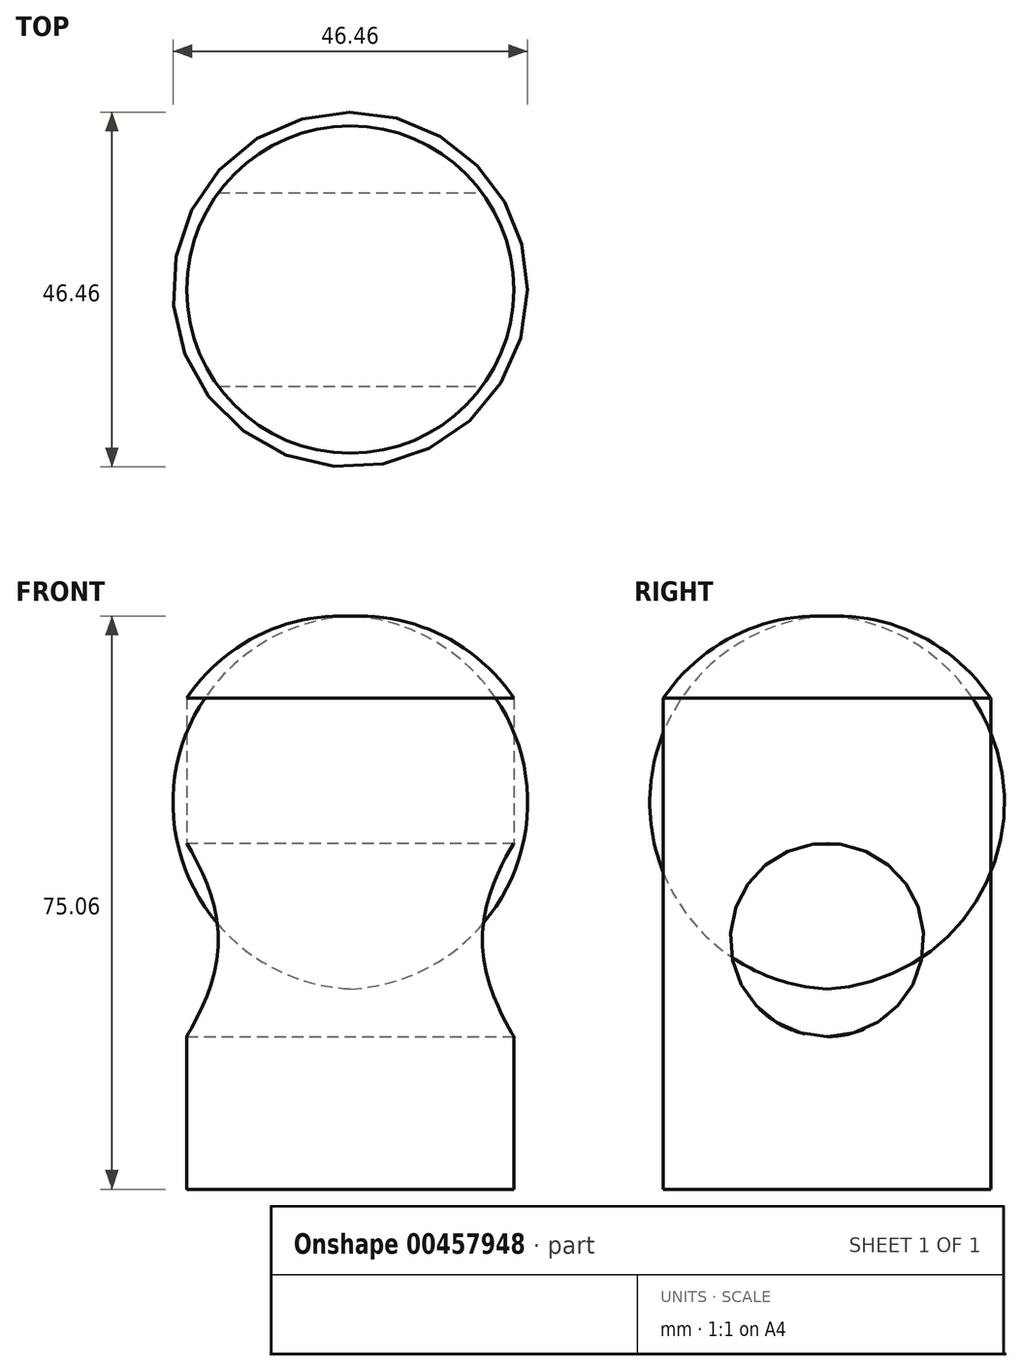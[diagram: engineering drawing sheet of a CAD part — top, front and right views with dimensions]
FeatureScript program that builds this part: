
annotation { "Feature Type Name" : "Feature", "Feature Type Description" : "" }
export const myFeature = defineFeature(function(context is Context, id is Id, definition is map)
    precondition{}
    {
        {
            var Q0;
            Q0=qCreatedBy(makeId("Front.planeOp"),FACE);
            var sketch = newSketch(context, id + "F0", { "sketchPlane" : qUnion([Q0])});
            skLineSegment(sketch, "E0", {"start": v(0, 31.65) * mm, "end": v(0, -32.66) * mm});
            skLineSegment(sketch, "E1", {"start": v(0, -32.66) * mm, "end": v(-21.44, -32.66) * mm});
            skLineSegment(sketch, "E2", {"start": v(-21.44, -32.66) * mm, "end": v(-21.44, 31.65) * mm});
            skLineSegment(sketch, "E3", {"start": v(-21.44, 31.65) * mm, "end": v(0, 31.65) * mm});
            skLineSegment(sketch, "E4", {"start": v(0, 31.65) * mm, "end": v(0, 42.37) * mm});
            skArc(sketch, "E5", {"start": v(0, 42.37) * mm, "mid": v(-12.12, 39.82) * mm, "end": v(-21.44, 31.65) * mm});
            skSolve(sketch);
        }
        {
            var Q0;
            Q0=makeQuery(id+"F0.imprint","IMPRINT",FACE,{"disambiguationData":[TD([[makeQuery(id+"F0.imprint","IMPRINT",EDGE,{"derivedFrom":sQuery(id+"F0.wireOp",EDGE,"E3")}),1.0]])]});
            var Q1;
            Q1=makeQuery(id+"F0.imprint","IMPRINT",FACE,{"disambiguationData":[TD([[makeQuery(id+"F0.imprint","IMPRINT",EDGE,{"derivedFrom":sQuery(id+"F0.wireOp",EDGE,"E0")}),-1.0]])]});
            var Q2;
            Q2=sQuery(id+"F0.wireOp",EDGE,"E4");
            revolve(context, id + "F1", {"entities" : qUnion([Q0, Q1]), "axis" : qUnion([Q2]), "revolveType" : RevolveType.FULL});
        }
        {
            var Q0;
            Q0=makeQuery(id+"F1.opRevolve","SWEPT_FACE",FACE,{"disambiguationData":[OSD([sQuery(id+"F0.wireOp",EDGE,"E2")])]});
            cPlane(context, id + "F2", {"entities" : qUnion([Q0]), "cplaneType" : CPlaneType.LINE_ANGLE, "offset" : 25.4 * mm, "angle" : 0 * degree, "width" : 152.4 * mm, "height" : 152.4 * mm});
        }
        {
            var Q0;
            Q0=qCreatedBy(id+"F2.planeOp",FACE);
            var sketch = newSketch(context, id + "F3", { "sketchPlane" : qUnion([Q0])});
            skCircle(sketch, "E6", {"center": v(0, 0) * mm, "radius": 12.67 * mm});
            skSolve(sketch);
        }
        {
            var Q0;
            Q0 = qSketchRegion(id + "F3", true);
            extrude(context, id + "F4", {"entities" : qUnion([Q0]), "operationType" : NewBodyOperationType.REMOVE, "endBound" : BoundingType.SYMMETRIC, "depth" : 63.5 * mm, "offsetDistance" : 25.4 * mm});
        }
    });
